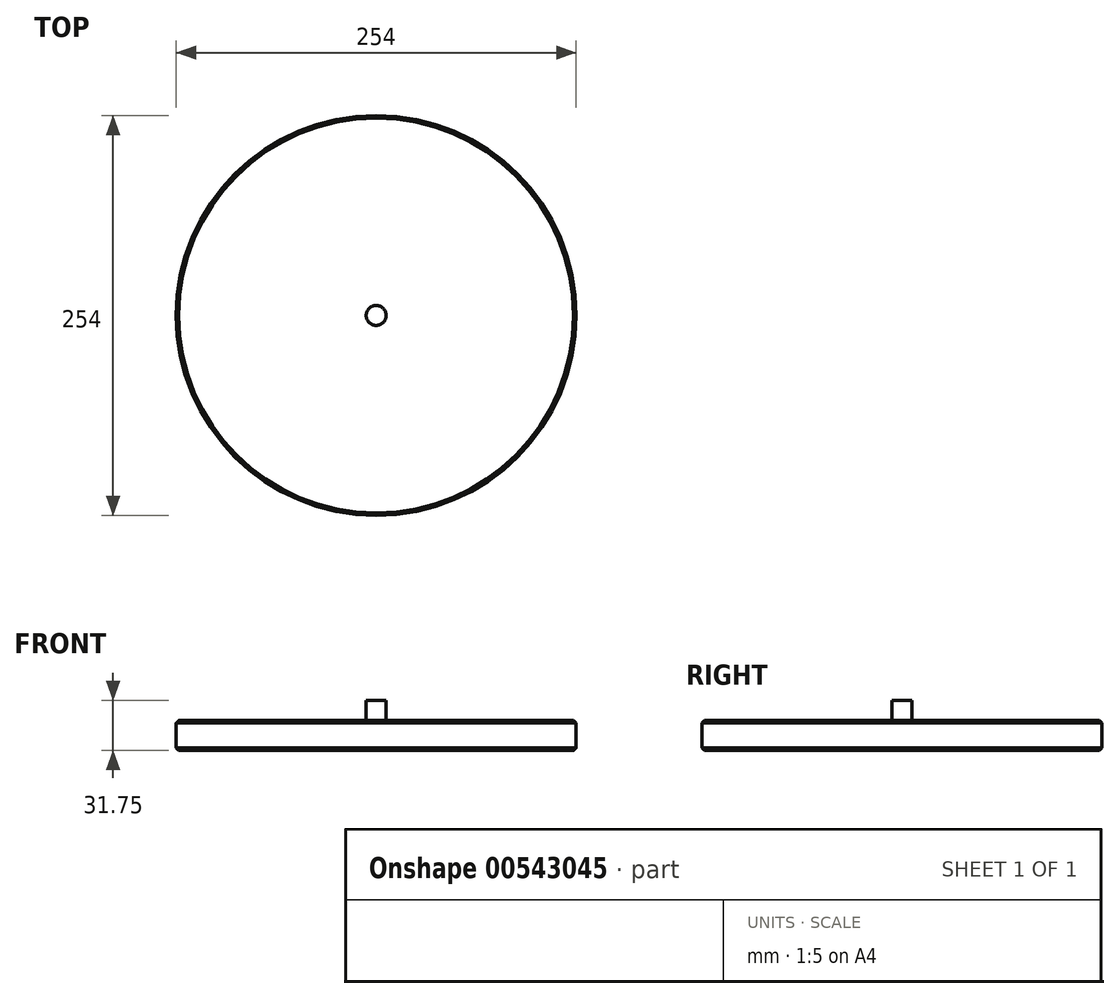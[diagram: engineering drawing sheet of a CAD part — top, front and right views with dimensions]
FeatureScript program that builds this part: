
annotation { "Feature Type Name" : "Feature", "Feature Type Description" : "" }
export const myFeature = defineFeature(function(context is Context, id is Id, definition is map)
    precondition{}
    {
        {
            var Q0;
            Q0=qCreatedBy(makeId("Right.planeOp"),FACE);
            var sketch = newSketch(context, id + "F0", { "sketchPlane" : qUnion([Q0])});
            skLineSegment(sketch, "E0", {"start": v(0, 0) * mm, "end": v(0, 19.05) * mm});
            skLineSegment(sketch, "E1", {"start": v(0, 19.05) * mm, "end": v(127, 19.05) * mm});
            skLineSegment(sketch, "E2", {"start": v(127, 19.05) * mm, "end": v(127, 0) * mm});
            skLineSegment(sketch, "E3", {"start": v(127, 0) * mm, "end": v(0, 0) * mm});
            skSolve(sketch);
        }
        {
            var Q0;
            Q0 = qSketchRegion(id + "F0", true);
            var Q1;
            Q1=sQuery(id+"F0.wireOp",EDGE,"E0");
            revolve(context, id + "F1", {"entities" : qUnion([Q0]), "axis" : qUnion([Q1]), "revolveType" : RevolveType.FULL});
        }
        {
            var Q0;
            Q0=makeQuery(id+"F1.opRevolve","SWEPT_EDGE",EDGE,{"disambiguationData":[OSD([sQuery(id+"F0.wireOp",EDGE,"E2"),sQuery(id+"F0.wireOp",EDGE,"E3")])]});
            var Q1;
            Q1=makeQuery(id+"F1.opRevolve","SWEPT_EDGE",EDGE,{"disambiguationData":[OSD([sQuery(id+"F0.wireOp",EDGE,"E1"),sQuery(id+"F0.wireOp",EDGE,"E2")])]});
            chamfer(context, id + "F2", {"entities" : qUnion([Q0, Q1]), "chamferType" : ChamferType.OFFSET_ANGLE, "width" : 1.59 * mm, "oppositeDirection" : false, "angle" : 45 * degree, "tangentPropagation" : true});
        }
        {
            var Q0;
            Q0=makeQuery(id+"F1.opRevolve","SWEPT_FACE",FACE,{"disambiguationData":[OSD([sQuery(id+"F0.wireOp",EDGE,"E1")])]});
            var sketch = newSketch(context, id + "F3", { "sketchPlane" : qUnion([Q0])});
            skCircle(sketch, "E4", {"center": v(0, 0) * mm, "radius": 6.35 * mm});
            skSolve(sketch);
        }
        {
            var Q0;
            Q0 = qSketchRegion(id + "F3", true);
            extrude(context, id + "F4", {"entities" : qUnion([Q0]), "operationType" : NewBodyOperationType.ADD, "depth" : 12.7 * mm, "offsetDistance" : 25.4 * mm});
        }
    });
